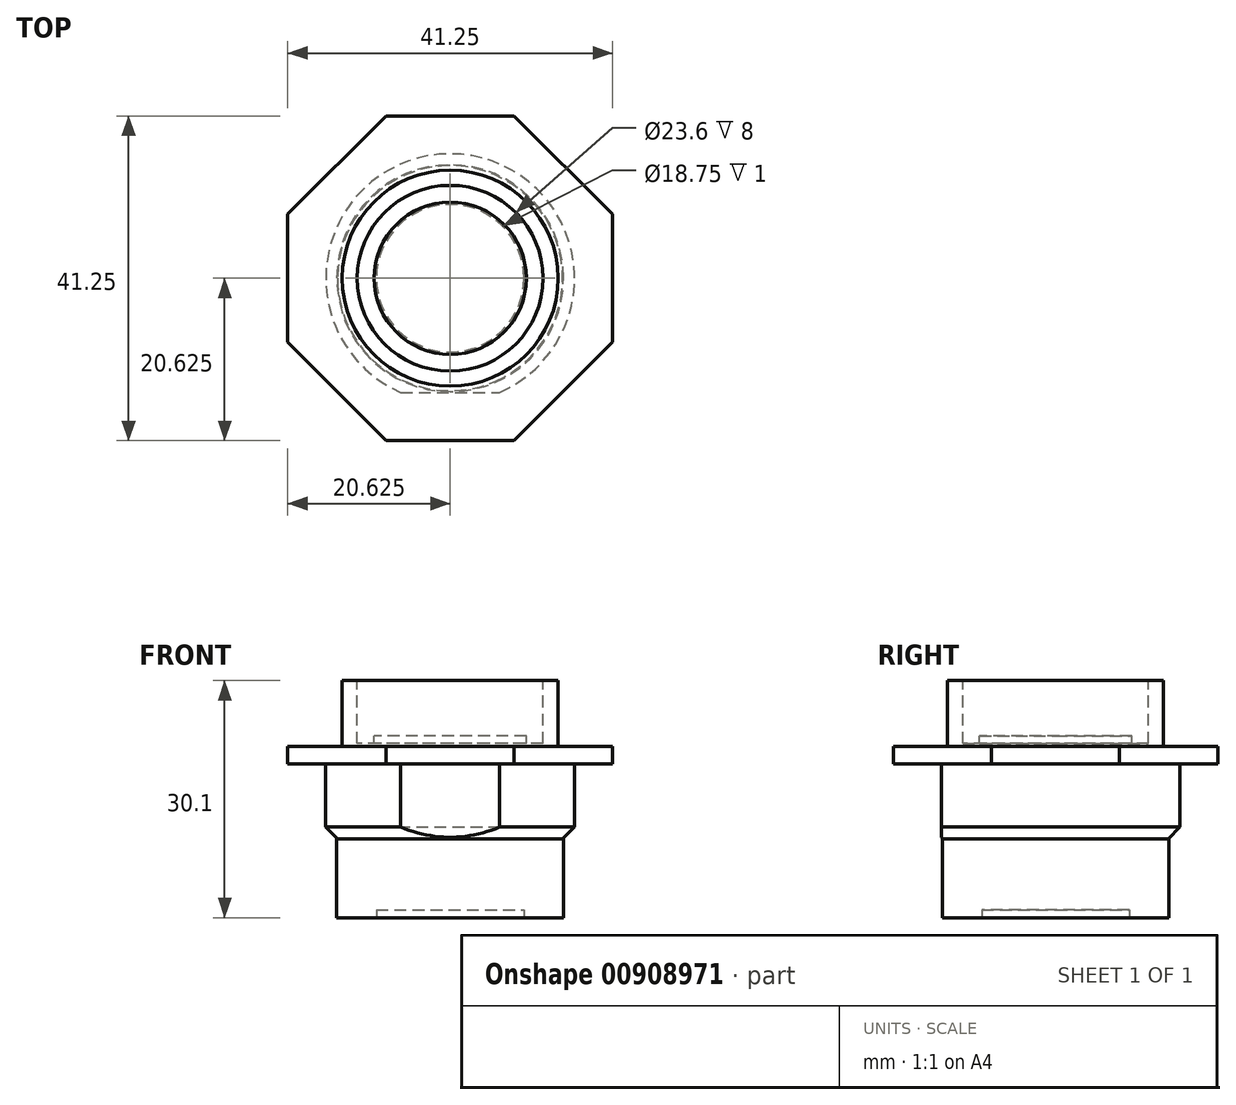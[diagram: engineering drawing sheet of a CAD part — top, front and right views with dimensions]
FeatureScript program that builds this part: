
annotation { "Feature Type Name" : "Feature", "Feature Type Description" : "" }
export const myFeature = defineFeature(function(context is Context, id is Id, definition is map)
    precondition{}
    {
        {
            var Q0;
            Q0=qCreatedBy(makeId("Top.planeOp"),FACE);
            var sketch = newSketch(context, id + "F0", { "sketchPlane" : qUnion([Q0])});
            skLineSegment(sketch, "E0.bottom", {"start": v(0, 0) * mm, "end": v(41.25, 0) * mm});
            skLineSegment(sketch, "E0.top", {"start": v(0, 41.25) * mm, "end": v(41.25, 41.25) * mm});
            skLineSegment(sketch, "E0.left", {"start": v(0, 0) * mm, "end": v(0, 41.25) * mm});
            skLineSegment(sketch, "E0.right", {"start": v(41.25, 0) * mm, "end": v(41.25, 41.25) * mm});
            skLineSegment(sketch, "E1", {"start": v(28.75, 41.25) * mm, "end": v(41.25, 28.75) * mm});
            skLineSegment(sketch, "E2", {"start": v(41.25, 12.5) * mm, "end": v(28.75, 0) * mm});
            skLineSegment(sketch, "E3", {"start": v(0, 12.5) * mm, "end": v(12.5, 0) * mm});
            skLineSegment(sketch, "E4", {"start": v(0, 28.75) * mm, "end": v(12.5, 41.25) * mm});
            skSolve(sketch);
        }
        {
            var Q0;
            {var subQ0=sQuery(id+"F0.wireOp",EDGE,"E1");Q0=makeQuery(id+"F0.imprint","IMPRINT",FACE,{"disambiguationData":[TD([[makeQuery(id+"F0.imprint","IMPRINT",EDGE,{"derivedFrom":subQ0}),-1.0]])]});}
            extrude(context, id + "F1", {"entities" : qUnion([Q0]), "depth" : 2.25 * mm, "offsetDistance" : 25 * mm});
        }
        {
            var Q0;
            Q0=qCreatedBy(makeId("Top.planeOp"),FACE);
            var sketch = newSketch(context, id + "F2", { "sketchPlane" : qUnion([Q0])});
            skCircle(sketch, "E5", {"center": v(20.62, 20.62) * mm, "radius": 13.71 * mm});
            skSolve(sketch);
        }
        {
            var Q0;
            Q0=makeQuery(id+"F2.imprint","IMPRINT",FACE,{"disambiguationData":[TD([[makeQuery(id+"F2.imprint","IMPRINT",EDGE,{"derivedFrom":sQuery(id+"F2.wireOp",EDGE,"E5")}),1.0]])]});
            extrude(context, id + "F3", {"entities" : qUnion([Q0]), "operationType" : NewBodyOperationType.ADD, "depth" : 10.6 * mm, "offsetDistance" : 25 * mm});
        }
        {
            var Q0;
            Q0=makeQuery(id+"F1.opExtrude","CAP_FACE",FACE,{"disambiguationData":[OSD([sQuery(id+"F0.wireOp",EDGE,"E0.bottom"),sQuery(id+"F0.wireOp",EDGE,"E0.top"),sQuery(id+"F0.wireOp",EDGE,"E0.left"),sQuery(id+"F0.wireOp",EDGE,"E0.right"),sQuery(id+"F0.wireOp",EDGE,"E1"),sQuery(id+"F0.wireOp",EDGE,"E2"),sQuery(id+"F0.wireOp",EDGE,"E3"),sQuery(id+"F0.wireOp",EDGE,"E4")])],"isStart":true});
            var sketch = newSketch(context, id + "F4", { "sketchPlane" : qUnion([Q0])});
            skCircle(sketch, "E6", {"center": v(20.62, -20.62) * mm, "radius": 15.8 * mm});
            skLineSegment(sketch, "E7", {"start": v(14.35, -6.12) * mm, "end": v(26.9, -6.12) * mm});
            skSolve(sketch);
        }
        {
            var Q0;
            {var subQ0=sQuery(id+"F4.wireOp",EDGE,"E7");Q0=makeQuery(id+"F4.imprint","IMPRINT",FACE,{"disambiguationData":[TD([[makeQuery(id+"F4.imprint","IMPRINT",EDGE,{"derivedFrom":subQ0}),-1.0]])]});}
            extrude(context, id + "F5", {"entities" : qUnion([Q0]), "operationType" : NewBodyOperationType.ADD, "depth" : 9.5 * mm, "offsetDistance" : 25 * mm});
        }
        {
            var Q0;
            Q0=makeQuery(id+"F5.opExtrude","CAP_EDGE",EDGE,{"disambiguationData":[OSD([sQuery(id+"F4.wireOp",EDGE,"E6")])],"isStart":false});
            chamfer(context, id + "F6", {"entities" : qUnion([Q0]), "width" : 1.5 * mm, "tangentPropagation" : true});
        }
        {
            var Q0;
            Q0=makeQuery(id+"F5.opExtrude","CAP_FACE",FACE,{"disambiguationData":[OSD([sQuery(id+"F4.wireOp",EDGE,"E6"),sQuery(id+"F4.wireOp",EDGE,"E7")])],"isStart":false});
            var sketch = newSketch(context, id + "F7", { "sketchPlane" : qUnion([Q0])});
            skCircle(sketch, "E8", {"center": v(20.62, -20.62) * mm, "radius": 14.4 * mm});
            skSolve(sketch);
        }
        {
            var Q0;
            Q0=qSketchRegion(id+"F7",true);
            extrude(context, id + "F8", {"entities" : qUnion([Q0]), "operationType" : NewBodyOperationType.ADD, "depth" : 10 * mm, "offsetDistance" : 25 * mm});
        }
        {
            var Q0;
            Q0=makeQuery(id+"F3.opExtrude","CAP_FACE",FACE,{"disambiguationData":[OSD([sQuery(id+"F2.wireOp",EDGE,"E5")])],"isStart":false});
            var sketch = newSketch(context, id + "F9", { "sketchPlane" : qUnion([Q0])});
            skCircle(sketch, "E9", {"center": v(20.62, 20.62) * mm, "radius": 11.8 * mm});
            skSolve(sketch);
        }
        {
            var Q0;
            Q0=qSketchRegion(id+"F9",true);
            extrude(context, id + "F10", {"entities" : qUnion([Q0]), "operationType" : NewBodyOperationType.REMOVE, "oppositeDirection" : true, "depth" : 7 * mm, "offsetDistance" : 25 * mm});
        }
        {
            var Q0;
            Q0=makeQuery(id+"F3.opExtrude","CAP_FACE",FACE,{"disambiguationData":[OSD([sQuery(id+"F2.wireOp",EDGE,"E5")])],"isStart":false});
            var sketch = newSketch(context, id + "F11", { "sketchPlane" : qUnion([Q0])});
            skCircle(sketch, "E10", {"center": v(20.62, 20.62) * mm, "radius": 9.67 * mm});
            skSolve(sketch);
        }
        {
            var Q0;
            Q0=makeQuery(id+"F11.imprint","IMPRINT",FACE,{"disambiguationData":[TD([[makeQuery(id+"F11.imprint","IMPRINT",EDGE,{"derivedFrom":sQuery(id+"F11.wireOp",EDGE,"E10")}),-1.0]])]});
            extrude(context, id + "F12", {"entities" : qUnion([Q0]), "operationType" : NewBodyOperationType.REMOVE, "oppositeDirection" : true, "depth" : 8 * mm, "offsetDistance" : 25 * mm});
        }
        {
            var Q0;
            Q0=makeQuery(id+"F8.opExtrude","CAP_FACE",FACE,{"disambiguationData":[OSD([sQuery(id+"F7.wireOp",EDGE,"E8")])],"isStart":false});
            var sketch = newSketch(context, id + "F13", { "sketchPlane" : qUnion([Q0])});
            skCircle(sketch, "E11", {"center": v(20.62, -20.62) * mm, "radius": 9.38 * mm});
            skSolve(sketch);
        }
        {
            var Q0;
            Q0=qSketchRegion(id+"F13",true);
            extrude(context, id + "F14", {"entities" : qUnion([Q0]), "operationType" : NewBodyOperationType.REMOVE, "oppositeDirection" : true, "depth" : 1 * mm, "offsetDistance" : 25 * mm});
        }
    });
